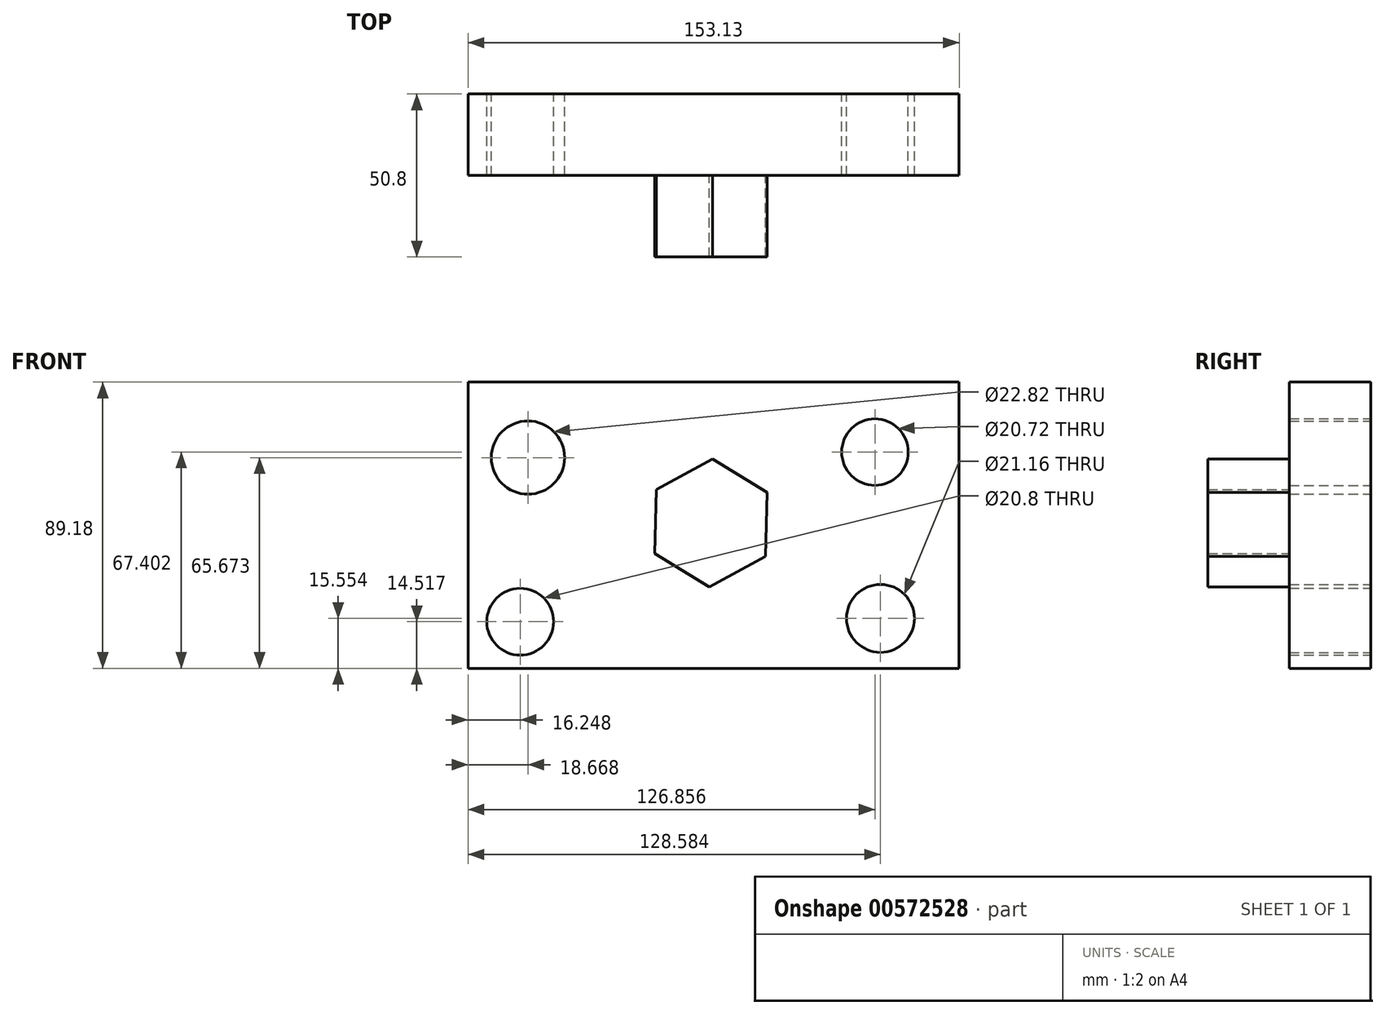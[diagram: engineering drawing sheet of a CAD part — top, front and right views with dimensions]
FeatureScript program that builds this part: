
annotation { "Feature Type Name" : "Feature", "Feature Type Description" : "" }
export const myFeature = defineFeature(function(context is Context, id is Id, definition is map)
    precondition{}
    {
        {
            var Q0;
            Q0=qCreatedBy(makeId("Front.planeOp"),FACE);
            var sketch = newSketch(context, id + "F0", { "sketchPlane" : qUnion([Q0])});
            skLineSegment(sketch, "E0.bottom", {"start": v(-75.7, 43.9) * mm, "end": v(77.43, 43.9) * mm});
            skLineSegment(sketch, "E0.top", {"start": v(-75.7, -45.28) * mm, "end": v(77.43, -45.28) * mm});
            skLineSegment(sketch, "E0.left", {"start": v(-75.7, 43.9) * mm, "end": v(-75.7, -45.28) * mm});
            skLineSegment(sketch, "E0.right", {"start": v(77.43, 43.9) * mm, "end": v(77.43, -45.28) * mm});
            skCircle(sketch, "E1", {"center": v(-57.03, 20.4) * mm, "radius": 11.41 * mm});
            skCircle(sketch, "E2", {"center": v(51.16, 22.12) * mm, "radius": 10.36 * mm});
            skCircle(sketch, "E3", {"center": v(52.88, -29.73) * mm, "radius": 10.58 * mm});
            skCircle(sketch, "E4", {"center": v(-59.45, -30.76) * mm, "radius": 10.4 * mm});
            skSolve(sketch);
        }
        {
            var Q0;
            Q0=makeQuery(id+"F0.imprint","IMPRINT",FACE,{"disambiguationData":[TD([[makeQuery(id+"F0.imprint","IMPRINT",EDGE,{"derivedFrom":sQuery(id+"F0.wireOp",EDGE,"E0.bottom")}),-1.0]])]});
            extrude(context, id + "F1", {"entities" : qUnion([Q0]), "depth" : 25.4 * mm, "offsetDistance" : 25.4 * mm});
        }
        {
            var Q0;
            Q0=makeQuery(id+"F1.opExtrude","CAP_FACE",FACE,{"disambiguationData":[OSD([sQuery(id+"F0.wireOp",EDGE,"E0.bottom"),sQuery(id+"F0.wireOp",EDGE,"E0.top"),sQuery(id+"F0.wireOp",EDGE,"E0.left"),sQuery(id+"F0.wireOp",EDGE,"E0.right"),sQuery(id+"F0.wireOp",EDGE,"E1"),sQuery(id+"F0.wireOp",EDGE,"E2"),sQuery(id+"F0.wireOp",EDGE,"E3"),sQuery(id+"F0.wireOp",EDGE,"E4")])],"isStart":false});
            var sketch = newSketch(context, id + "F2", { "sketchPlane" : qUnion([Q0])});
            skCircle(sketch, "E5.cCircle", {"center": v(0, 0) * mm, "radius": 17.29 * mm, "construction": true});
            skLineSegment(sketch, "E5.0", {"start": v(0.52, 19.95) * mm, "end": v(17.54, 9.53) * mm});
            skLineSegment(sketch, "E5.1", {"start": v(17.54, 9.53) * mm, "end": v(17.02, -10.43) * mm});
            skLineSegment(sketch, "E5.2", {"start": v(17.02, -10.43) * mm, "end": v(-0.52, -19.95) * mm});
            skLineSegment(sketch, "E5.3", {"start": v(-0.52, -19.95) * mm, "end": v(-17.54, -9.53) * mm});
            skLineSegment(sketch, "E5.4", {"start": v(-17.54, -9.53) * mm, "end": v(-17.02, 10.43) * mm});
            skLineSegment(sketch, "E5.5", {"start": v(-17.02, 10.43) * mm, "end": v(0.52, 19.95) * mm});
            skPoint(sketch, "E5.0.midPoint", {"position": v(9.03, 14.74) * mm});
            skSolve(sketch);
        }
        {
            var Q0;
            Q0 = qSketchRegion(id + "F2", true);
            extrude(context, id + "F3", {"entities" : qUnion([Q0]), "operationType" : NewBodyOperationType.ADD, "depth" : 25.4 * mm, "offsetDistance" : 25.4 * mm});
        }
    });
